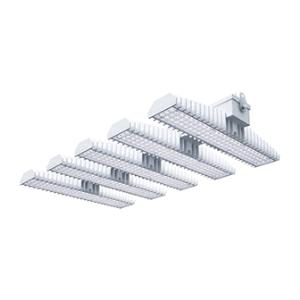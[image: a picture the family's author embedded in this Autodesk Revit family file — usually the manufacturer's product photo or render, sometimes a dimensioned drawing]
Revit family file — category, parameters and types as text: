
# Revit family: 3f_filippi_-_3f_lem_medio_3f_filippi_-_58915_a0811_-_3f_lem_5_led_250_dali_cr_medio___vt_3903
name_source: partatom
category: Lighting Fixtures
units: mm (PartAtom-declared; Revit-internal decimal feet)

## family parameters
Cut with Voids When Loaded = No
Host = Face
Light Source = No
Part Type = Normal
Room Calculation Point = No
Round Connector Dimension = Use Diameter
Shared = No

## types (1)
- 3F Filippi - 3F LEM Medio (1 x LED, 38698 lm, 274 W, 4000 K)
    Apparent Load = 274 VA
    Approval mark = CE
    CIE Flux Codes = 83 96 99 100 100
    Color Rendering = 80
    Color Temperature = 4000 K
    Control Gear = Electronic transformer
    Default Elevation = 1800 mm
    Description = Industrial luminaire with high light output and high luminous efficiency designed with the most innovative technologies for environments with temperature up to 55°C.

ILLUMINOTECHNICAL
Luminous efficiency 100% (DLOR 99%, ULOR 1%).
Initial luminous flux of the luminaire 38698 lm.
Medium distribution with rectangular shape.
Installation Interdistance Transv.D = 1.02 x hu - Long.D = 1.06 x hu.
Tabular UGR (CIE 117 - 4H-8H; S=0.25H; 70/50/20): RUG 18.9 - 18.5.
Beam angle: 65° - 67°.
Luminous efficacy 141 lm/W.
Lifetime (L93/B10): 30000 h. (tq+25°C)
Lifetime (L90/B10): 50000 h. (tq+25°C)
Lifetime (L85/B10): 80000 h. (tq+25°C)
Lifetime (L80/B10): 100000 h. (tq+25°C)
Lifetime (L85/B10): 50000 h. (tq+55°C)
Sudden decreased luminous flux after 50000 hours: 0% (C0).
Photobiological safety in compliance with IEC/TR 62778: RG0 risk exempt, (IEC 62471).
In compliance with IEC/EN 62722-2-1 - IEC/EN 62717 standards.

SOURCE
5 Mid-Power linear LED modules 50W/840.
Energy efficiency class (UE 2019/2020 - UE 2019/2015): C.
CIE 13.3 Colour rendering index: CRI >80 (R9 <50%).
IES TM-30 Fidelity Index: Rf = 84 Rg = 95.
CCT nominal colour temperature 4000 K.
Colour initial tolerance (MacAdam): SDCM 3.

MECHANICAL
Passive modular heatsinks in die-casted aluminium, painted in white colour.
To optimize the thermal management of the LED module, the heatsinks are oversized and provided with self-cleaning of cooling fins.
Wiring body in aluminium and galvanised steel anchored solidly to the sinks and thermally separated.
3F Lens lenses with high luminous efficiency, transparent methacrylate (PMMA), fixed to the LED modules.
Fixing brackets in stainless steel.
Luminaire with limited surface temperature. - D - (EN 60598-2-24)
Dimensions: 952x542 mm, height 133 mm. Weight 23.385 kg.
IP65 protection degree.
Mechanical strength to impacts IK06 (1 joule).
Glow-wire test resistance 650°C.

ELECTRICAL
Halogen Free DALI-2 DATI (Parts 251, 252, 253), PUSH-DIM, electronic wiring 230V-50/60Hz, power factor 0.97 at full load, THD <25%, constant output current, class I, 3 driver, 3 DALI addresses.
Power of the luminaire 274 W.
ENEC - CE.
SAFE FLICKER: PstLM=<1 and SVM=<0.4 (IEC TR 61547-1 and IEC TR 63158), to ensure a more comfortable and safe light.
Luminaire compliant with EN 60598-2-22 for power supply from a centralised emergency system CPSS (Central Power Supply System), not incorporated in the luminaire - high risk areas excluded. The default power and flux are 100% in AC and 15% in DC.
Ambient temperature from -30°C to +55°C.
Temperature class T6 max 85°C.
Quick connection via M25 5P connector with 9-13 mm tightening range.
Power unit positioned on a separate compartment by the LED module to ensure optimum temperatures of cabling components, to be inspectable and maintainable.
Relative humidity UR: <85%.

INSTALLATION
Ceiling / Suspended / Wall.
All accessories dedicated to this product are available on the Catalog and on our website www.3F-Filippi.com.

ACCESSORIES
A0811 - VT transparent glass, tempered, not flammable, with sealing gasket.
One required for each light module. The pack contains 10 pieces.

APPLICATIONS
In commercial environments, exhibition and industrial areas, stores, open areas.
Applications with high ambient temperature up to 55°C.
Environments in which it is necessary a total protection against falling fragments (eg environments with foodstuffs or machines with moving parts or with extreme temperature changes), use luminaires with polycarbonate lenses.

LIGHT MANAGEMENT
Recommended minimum setting: 10%.
The luminaire, equipped with (DALI-2 DATI) driver, can be controlled manually with 3F Easy Dim technology or automatically/manually with wired or wireless DALI/D2D control systems.
The D2D driver guarantees interoperability with other devices with the same certification by making the following information available:
Device Data (Part 251), Energy Report (Part 252), Diagnosis & Maintenance (Part 253).
In electrical systems without a regulation system (manual or automatic) and DALI bus, a suitable jumper must be made on the DA-DA terminals of the appliance.

WARNING
Fixture not suitable for cold stores with an ambient temperature <0°C and/or relative humidity >85%.
Luminaire designed for disposal/recycling at end-of-life.
Replaceable (LED only) light source by a professional. Replaceable control gear by a professional.
    Height = 133 mm  [stored 0.436352 ft]
    Lamp = 1 x LED
    Lamp Light Flux = 38698 lm
    Lamp Power = 274 W
    Lamp count = 1
    Length = 952 mm
    Lifetime = 50000 h
    Luminous efficacy = 141 lm/W
    Manufacturer = 3F Filippi
    ModVariant = No
    Model = 3F Filippi - 58915+A0811 - 3F LEM 5 LED 250 DALI CR MEDIO + VT
    Mounting Place = Ceiling
    Mounting Type = Pendant
    Number of Poles = 1
    OnlyDefault = Yes
    Power Factor = 1
    Product Name = 3F Filippi - 3F LEM Medio
    Product group = pendant luminaire
    ProductGroupID = 9
    Protection Class = Protection class I
    Protection Degree = IP 65
    RLX_Detail_Level = 1
    RLX_Emergency_Light_Flux = 0 lm
    RLX_Emergency_Type = 0
    RLX_Emergency_Type_DB = No
    RlxData = <blob elided: 129065 chars, md5=d278fb31>
    Socket = socket
    Standby Power = 0 W
    System Light Flux = 38698 lm
    System Power = 274 W
    Type Comments = Product without accessories
    Type Image = 3f_filippi_-_lem_5__a0811.jpg
    URL = http://relux.com
    VarID = ---
    Voltage = 0 V
    Weight = 0.00 kg
    Width = 542 mm

note: [stored X ft] marks values corroborated as IEEE doubles in the binary element streams (Revit-internal decimal feet)

## geometry (parser evidence)
native form markers: Blend x4, Sweep x10
no freeform markers — native parametric forms only
